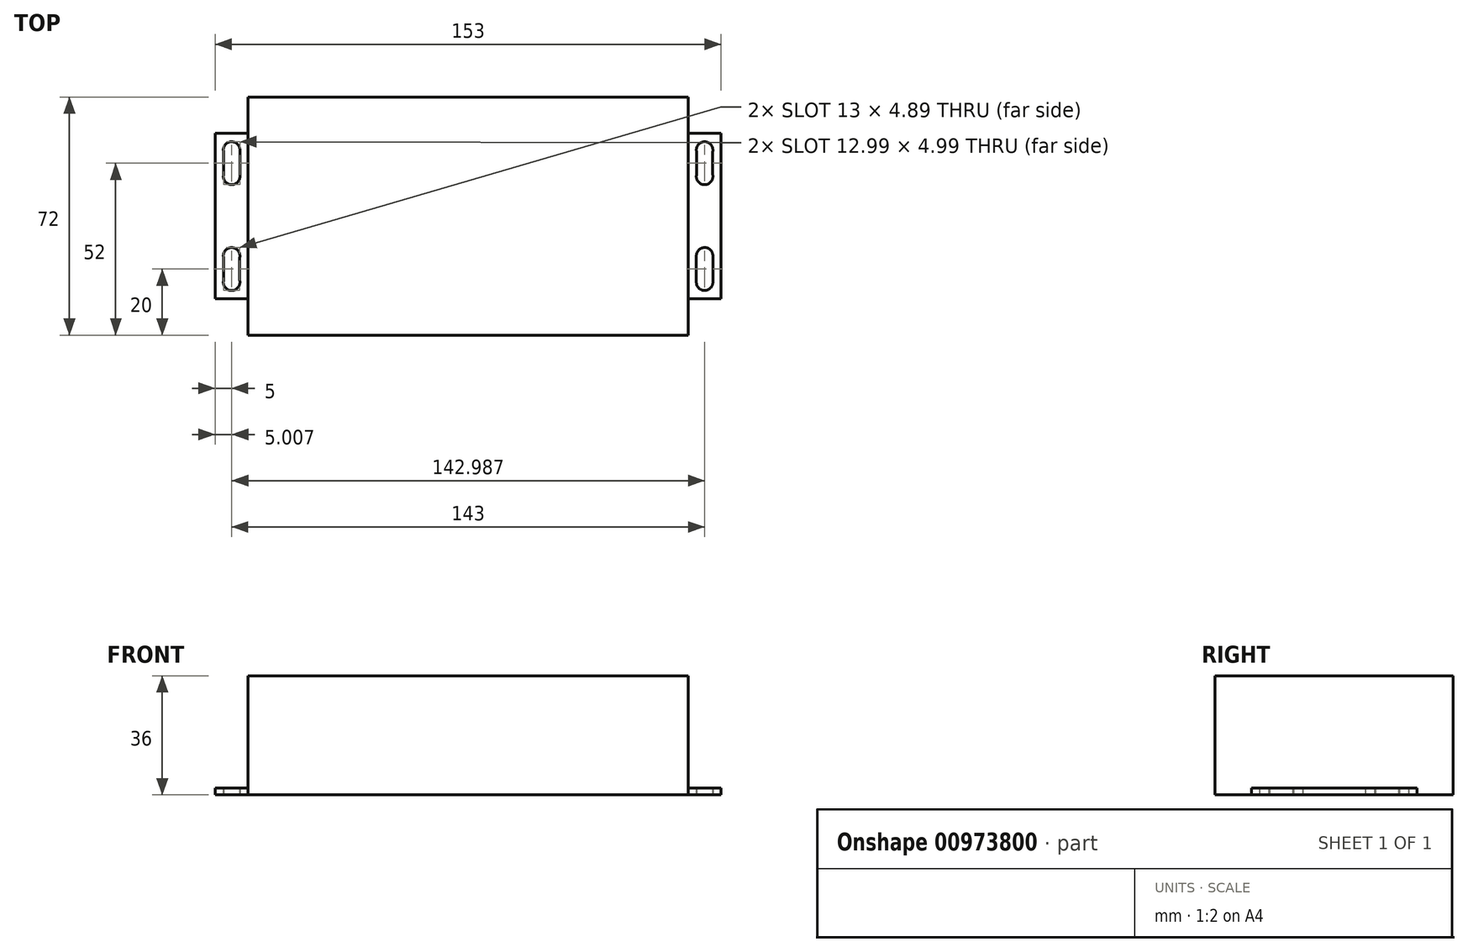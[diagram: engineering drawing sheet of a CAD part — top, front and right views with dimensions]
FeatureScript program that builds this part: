
annotation { "Feature Type Name" : "Feature", "Feature Type Description" : "" }
export const myFeature = defineFeature(function(context is Context, id is Id, definition is map)
    precondition{}
    {
        {
            var Q0;
            Q0=qCreatedBy(makeId("Top.planeOp"),FACE);
            var sketch = newSketch(context, id + "F0", { "sketchPlane" : qUnion([Q0])});
            skLineSegment(sketch, "E0.bottom", {"start": v(-66.5, -36) * mm, "end": v(66.5, -36) * mm});
            skLineSegment(sketch, "E0.top", {"start": v(-66.5, 36) * mm, "end": v(66.5, 36) * mm});
            skLineSegment(sketch, "E0.left", {"start": v(-66.5, -36) * mm, "end": v(-66.5, 36) * mm});
            skLineSegment(sketch, "E0.right", {"start": v(66.5, -36) * mm, "end": v(66.5, 36) * mm});
            skPoint(sketch, "E0.middle", {"position": v(0, 0) * mm});
            skSolve(sketch);
        }
        {
            var Q0;
            Q0 = qSketchRegion(id + "F0", true);
            extrude(context, id + "F1", {"entities" : qUnion([Q0]), "depth" : 36 * mm, "offsetDistance" : 25 * mm});
        }
        {
            var Q0;
            Q0=makeQuery(id+"F1.opExtrude","CAP_FACE",FACE,{"disambiguationData":[OSD([sQuery(id+"F0.wireOp",EDGE,"E0.bottom"),sQuery(id+"F0.wireOp",EDGE,"E0.top"),sQuery(id+"F0.wireOp",EDGE,"E0.left"),sQuery(id+"F0.wireOp",EDGE,"E0.right")])],"isStart":true});
            var sketch = newSketch(context, id + "F2", { "sketchPlane" : qUnion([Q0])});
            skLineSegment(sketch, "E1.bottom", {"start": v(-66.5, 25) * mm, "end": v(-76.5, 25) * mm});
            skLineSegment(sketch, "E1.top", {"start": v(-66.5, -25) * mm, "end": v(-76.5, -25) * mm});
            skLineSegment(sketch, "E1.left", {"start": v(-66.5, 25) * mm, "end": v(-66.5, -25) * mm});
            skLineSegment(sketch, "E1.right", {"start": v(-76.5, 25) * mm, "end": v(-76.5, -25) * mm});
            skLineSegment(sketch, "E2", {"start": v(-66.5, 0) * mm, "end": v(-71.5, 0) * mm, "construction": true});
            skPoint(sketch, "E2.endSnap0", {"position": v(-71.5, 25) * mm});
            skLineSegment(sketch, "E3", {"start": v(-71.5, 0) * mm, "end": v(-71.5, 12) * mm, "construction": true});
            skLineSegment(sketch, "E4", {"start": v(-71.5, 0) * mm, "end": v(-71.5, -12) * mm, "construction": true});
            skLineSegment(sketch, "E5", {"start": v(-71.5, -12) * mm, "end": v(-71.5, -20) * mm, "construction": true});
            skLineSegment(sketch, "E6", {"start": v(-71.5, 12) * mm, "end": v(-71.5, 20) * mm, "construction": true});
            skArc(sketch, "E7", {"start": v(-69.06, 19.48) * mm, "mid": v(-71.5, 22.5) * mm, "end": v(-73.94, 19.48) * mm});
            skArc(sketch, "E8", {"start": v(-73.94, 12.52) * mm, "mid": v(-71.5, 9.5) * mm, "end": v(-69.06, 12.52) * mm});
            skArc(sketch, "E9", {"start": v(-73.99, -19.75) * mm, "mid": v(-71.63, -22.5) * mm, "end": v(-69, -20) * mm});
            skArc(sketch, "E10", {"start": v(-69, -12) * mm, "mid": v(-71.63, -9.5) * mm, "end": v(-73.99, -12.25) * mm});
            skLineSegment(sketch, "E11", {"start": v(-73.94, 12.52) * mm, "end": v(-73.94, 19.48) * mm});
            skLineSegment(sketch, "E12", {"start": v(-69.06, 12.52) * mm, "end": v(-69.06, 19.48) * mm});
            skLineSegment(sketch, "E13", {"start": v(-73.99, -19.75) * mm, "end": v(-73.99, -11.75) * mm});
            skLineSegment(sketch, "E14", {"start": v(-69, -20) * mm, "end": v(-69, -12) * mm});
            skSolve(sketch);
        }
        {
            var Q0;
            Q0 = qSketchRegion(id + "F2", true);
            extrude(context, id + "F3", {"entities" : qUnion([Q0]), "operationType" : NewBodyOperationType.ADD, "oppositeDirection" : true, "depth" : 2 * mm, "offsetDistance" : 25 * mm});
        }
        {
            var Q0;
            Q0=makeQuery(id+"F3.boolean.opBoolean","MERGE",FACE,{"derivedFrom":[makeQuery(id+"F1.opExtrude","CAP_FACE",FACE,{"disambiguationData":[OSD([sQuery(id+"F0.wireOp",EDGE,"E0.bottom"),sQuery(id+"F0.wireOp",EDGE,"E0.top"),sQuery(id+"F0.wireOp",EDGE,"E0.left"),sQuery(id+"F0.wireOp",EDGE,"E0.right")])],"isStart":true}),makeQuery(id+"F3.opExtrude","CAP_FACE",FACE,{"disambiguationData":[OSD([sQuery(id+"F2.wireOp",EDGE,"E1.bottom"),sQuery(id+"F2.wireOp",EDGE,"E1.top"),sQuery(id+"F2.wireOp",EDGE,"E1.left"),sQuery(id+"F2.wireOp",EDGE,"E1.right"),sQuery(id+"F2.wireOp",EDGE,"E7"),sQuery(id+"F2.wireOp",EDGE,"E8"),sQuery(id+"F2.wireOp",EDGE,"E9"),sQuery(id+"F2.wireOp",EDGE,"E10"),sQuery(id+"F2.wireOp",EDGE,"E11"),sQuery(id+"F2.wireOp",EDGE,"E12"),sQuery(id+"F2.wireOp",EDGE,"E13"),sQuery(id+"F2.wireOp",EDGE,"E14")])],"isStart":true})]});
            var sketch = newSketch(context, id + "F4", { "sketchPlane" : qUnion([Q0])});
            skLineSegment(sketch, "E15.bottom", {"start": v(66.5, -25) * mm, "end": v(76.5, -25) * mm});
            skLineSegment(sketch, "E15.top", {"start": v(66.5, 25) * mm, "end": v(76.5, 25) * mm});
            skLineSegment(sketch, "E15.left", {"start": v(66.5, -25) * mm, "end": v(66.5, 25) * mm});
            skLineSegment(sketch, "E15.right", {"start": v(76.5, -25) * mm, "end": v(76.5, 25) * mm});
            skLineSegment(sketch, "E16", {"start": v(66.5, 0) * mm, "end": v(71.5, 0) * mm, "construction": true});
            skPoint(sketch, "E16.endSnap0", {"position": v(71.5, -25) * mm});
            skLineSegment(sketch, "E17", {"start": v(71.5, 0) * mm, "end": v(71.5, -12) * mm, "construction": true});
            skLineSegment(sketch, "E18", {"start": v(71.5, 0) * mm, "end": v(71.5, 12) * mm, "construction": true});
            skLineSegment(sketch, "E19", {"start": v(71.5, 12) * mm, "end": v(71.5, 20) * mm, "construction": true});
            skLineSegment(sketch, "E20", {"start": v(71.5, -12) * mm, "end": v(71.5, -20) * mm, "construction": true});
            skArc(sketch, "E21", {"start": v(69.06, -19.48) * mm, "mid": v(71.5, -22.5) * mm, "end": v(73.94, -19.48) * mm});
            skArc(sketch, "E22", {"start": v(73.94, -12.52) * mm, "mid": v(71.5, -9.5) * mm, "end": v(69.06, -12.52) * mm});
            skArc(sketch, "E23", {"start": v(73.99, 19.75) * mm, "mid": v(71.63, 22.5) * mm, "end": v(69, 20) * mm});
            skArc(sketch, "E24", {"start": v(69, 12) * mm, "mid": v(71.63, 9.5) * mm, "end": v(73.99, 12.25) * mm});
            skLineSegment(sketch, "E25", {"start": v(73.94, -12.52) * mm, "end": v(73.94, -19.48) * mm});
            skLineSegment(sketch, "E26", {"start": v(69.06, -12.52) * mm, "end": v(69.06, -19.48) * mm});
            skLineSegment(sketch, "E27", {"start": v(73.99, 19.75) * mm, "end": v(73.99, 11.75) * mm});
            skLineSegment(sketch, "E28", {"start": v(69, 20) * mm, "end": v(69, 12) * mm});
            skLineSegment(sketch, "E29", {"start": v(0, 0) * mm, "end": v(66.5, 0) * mm});
            skSolve(sketch);
        }
        {
            var Q0;
            Q0 = qSketchRegion(id + "F4", true);
            extrude(context, id + "F5", {"entities" : qUnion([Q0]), "operationType" : NewBodyOperationType.ADD, "oppositeDirection" : true, "depth" : 2 * mm, "offsetDistance" : 25 * mm});
        }
    });
